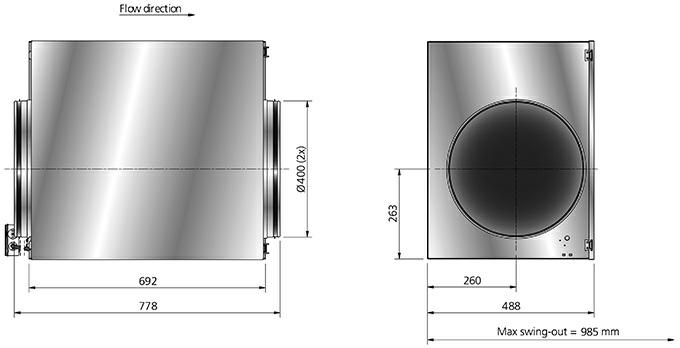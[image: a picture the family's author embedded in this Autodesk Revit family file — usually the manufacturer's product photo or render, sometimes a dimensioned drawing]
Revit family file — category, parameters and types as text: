
# Revit family: IRE 500 F3 ERP AC_7900046
name_source: partatom
category: Mechanical Equipment
revit_build: Autodesk Revit MEP 2014 (Build: 20130308_1515(x64)
units: mm (PartAtom-declared; Revit-internal decimal feet)

## types (1)
- IRE 500 F3 ERP AC
    Capacitor = - μF
    Current = 6 A
    Depth = 780 mm  [stored 2.55906 ft]
    Description = Insulated duct fans with circular connections
    Diameter = 500 mm  [stored 1.64042 ft]
    Frequency = 50 Hz
    Height = 584 mm  [stored 1.91601 ft]
    Main Material = Steel, Galvanized
    Max. temperature of transported air = 70 °C
    Max. temperature of transported air when speed controlled = 70 °C
    Phase = 3
    Power = 3400 W
    Sound pressure level at 3 m = 55 dB(A)
    Speed = 1390 rpm
    Voltage = 400 V
    Voltage range = 380-415 V
    Weight = 81.20 kg
    Width = 907 mm  [stored 2.97572 ft]
    Wiring diagram = Y 4040004 / Δ 4040003

note: [stored X ft] marks values corroborated as IEEE doubles in the binary element streams (Revit-internal decimal feet)

## geometry (parser evidence)
native form markers: Sweep x5
no freeform markers — native parametric forms only
